# Revit family: Gira_541400
name_source: partatom
category: Electrical Fixtures
revit_build: Autodesk Revit 2017 (Build: 20160225_1515(x64)
units: mm (PartAtom-declared; Revit-internal decimal feet)

## family parameters
Cut with Voids When Loaded = No
Host = Face
Maintain Annotation Orientation = Yes
Part Type = Normal
Room Calculation Point = No
Round Connector Dimension = Use Diameter
Shared = No

## types (1)
- S3000 Jal.steuereins. + Nebenst.eing. Einsatz
    Ausführung der Oberfläche = nicht zutreffend
    Aussperrsicherung = No
    Available = Yes
    Befestigungsart = Krallen-/Schraubbefestigung
    Category = Jalousiesteuerung
    Data sheet (1) = https://katalog.gira.de
    Default Elevation = 1219 mm
    Farbe = sonstige
    GTIN = 4010337027423
    Geeignet für Regensensor = No
    Geeignet für Schutzart (IP) = IP20
    Geeignet für Windsensor = No
    HAN = 541400
    Halogenfrei = No
    HeinzeBIM = https://bimportal.heinze.de
    Integrierte Zeitschaltuhr = No
    Keynote = Einsatz_1fach
    Manufacturer URL = https://www.gira.de
    Max. Schaltleistung = 1000 Voltampere
    Mit Astro-Programm = No
    Mit Glasbruchmelderanschluss = No
    Mit Helligkeitssensoranschluss = No
    Mit Memory-Funktion = No
    Montageart = unter Putz
    Name = S3000 Jal.steuereins. + Nebenst.eing. Einsatz
    Nebenstelleneingang = Yes
    Nennspannung = 230 Volt
    Oberfläche = sonstige
    Region = DE
    Transparent = No
    URL = http://katalog.gira.de
    Werkstoff = sonstige
    Werkstoffgüte = sonstige
    Zufallsgenerator = No
    Zusammenstellung = Basiselement

## geometry (parser evidence)
native form markers: Blend x2, Sweep x3
no freeform markers — native parametric forms only
